# Revit family: Malvestio_329504
name_source: partatom
category: Furniture
revit_build: Autodesk Revit Architecture 2014 (Build: 20131024_2115(x64)
units: mm (PartAtom-declared; Revit-internal decimal feet)

## types (1)
- Malvestio_329504
    BIMobject category = Other Furniture
    Date of publishing = 2014-10-30
    Depth = 700 mm  [stored 2.29659 ft]
    Description = Linkar emergency trolley, 60cm drawers, with defibrillator holder tray and IV pole.
    Design country = Italy
    Edition number = 1
    Height = 1000 mm  [stored 3.28084 ft]
    IFC Classification = Furniture
    Installation instructions = http://www.malvestio.it
    Manufacturer country = Italy
    Manufacturer name = Malvestio
    Manufacturer url = http://www.malvestio.it
    Material main = Plastic-Malvestio-329504-Laminated
    Material secondary = Stainless-Malvestio-329504-Steel
    Nominal height = 1000
    Nominal width = 890
    Product SKU = LINKAR-TROLLEYS-329504
    Product data url = http://www.malvestio.it
    QR code = http://malvestio.bimobject.com
    UNSPSC Code = 56
    UNSPSC Name = Furniture and Furnishings
    URL = http://malvestio.bimobject.com
    Weight Net (Kg) = 100
    Width = 890 mm  [stored 2.91995 ft]
    Youtube clip = http://www.malvestio.it

note: [stored X ft] marks values corroborated as IEEE doubles in the binary element streams (Revit-internal decimal feet)

## geometry (parser evidence)
native form markers: Sweep x3
no freeform markers — native parametric forms only
